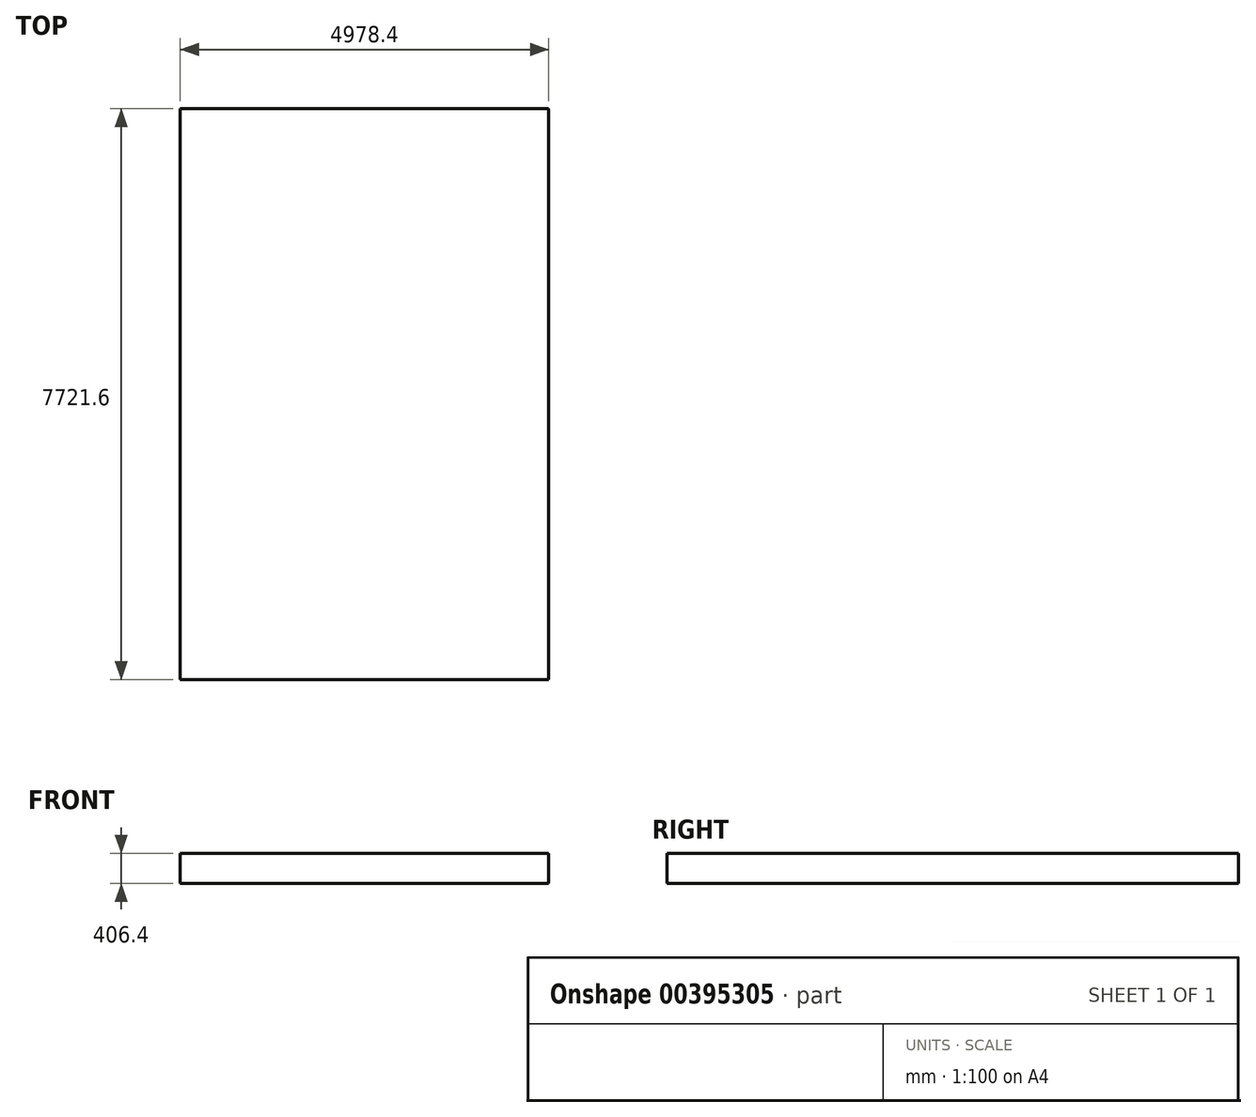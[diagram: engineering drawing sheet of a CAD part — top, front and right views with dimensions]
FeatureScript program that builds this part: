
annotation { "Feature Type Name" : "Feature", "Feature Type Description" : "" }
export const myFeature = defineFeature(function(context is Context, id is Id, definition is map)
    precondition{}
    {
        {
            var Q0;
            Q0=qCreatedBy(makeId("Top.planeOp"),FACE);
            var sketch = newSketch(context, id + "F0", { "sketchPlane" : qUnion([Q0])});
            skLineSegment(sketch, "E0.bottom", {"start": v(-2489.53, 5036.96) * mm, "end": v(2488.87, 5036.96) * mm});
            skLineSegment(sketch, "E0.top", {"start": v(-2489.53, -2684.64) * mm, "end": v(2488.87, -2684.64) * mm});
            skLineSegment(sketch, "E0.left", {"start": v(-2489.53, 5036.96) * mm, "end": v(-2489.53, -2684.64) * mm});
            skLineSegment(sketch, "E0.right", {"start": v(2488.87, 5036.96) * mm, "end": v(2488.87, -2684.64) * mm});
            skSolve(sketch);
        }
        {
            var Q0;
            Q0=qSketchRegion(id+"F0",true);
            extrude(context, id + "F1", {"entities" : qUnion([Q0]), "oppositeDirection" : true, "depth" : 406.4 * mm});
        }
    });
